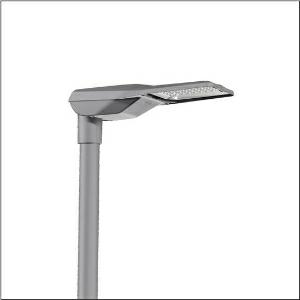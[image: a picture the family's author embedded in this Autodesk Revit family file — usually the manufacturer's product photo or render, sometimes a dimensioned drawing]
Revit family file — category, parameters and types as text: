
# Revit family: streetlight_sl_21_iq_mini___p1_0a_5xe2a31d08hb_09ea
name_source: partatom
category: Lighting Fixtures
units: mm (PartAtom-declared; Revit-internal decimal feet)

## family parameters
Cut with Voids When Loaded = No
Host = Face
Light Source = No
Part Type = Normal
Room Calculation Point = No
Round Connector Dimension = Use Diameter
Shared = No

## types (1)
- --- (1 x LED, 9450 lm, 70.9 W, 3000K)
    Apparent Load = 71 VA
    CIE Flux Codes = 21 50 90 100 100
    Color Rendering = 70
    Color Temperature = 3000K
    Default Elevation = 1800 mm
    Description = Streetlight SL 21 mini, mast luminaire, primary light control with lens, of PMMA, primary optical cover: cover, of toughened safety glass, transparent, light distribution: P1.0a, light emission: direct distribution, primary light characteristic: asymmetric, installation type: post-top, side-entry, LED, High Power LED, rated luminous flux: 9.450lm, luminous efficacy: 133lm/W, light colour: 730, colour temperature: 3000K, control gear: ECG iQ, control: Auto-Match, Temp-Guard, Lumen-Switch, Night-Set, Smart-Wire, Light-Fading, Desk-Remote (wireless, voltage-free reading and setting of iQ features in the workshop via application-optimized NFC function/RFID function), optimised constant luminous flux control (CLO 2.0), mains connection: 220..240V, AC, 50/60Hz, start of lifetime: 71W, end of lifetime: 75W, reduction: 31W, luminaire housing, of diecast aluminium, powder-coated, Siteco® metallic grey (DB 702S), corrosivity category C5 according to DIN EN ISO 12944, length: 628mm, width: 235mm, height: 110mm, spigot size: 60/76mm (post-top) and 42/60/76mm (side-entry), mast flange for spigot size: 42mm: 5XC10008XM4, 60mm: 5XC10008XM2, 76/60mm: 5XC10108XM1, protection rating (complete): IP66, insulation class (complete): insulation class II (safety insulation), certification: CE, ENEC, VDE, impact resistance: IK09, permissible operating ambient temperature for outdoor applications: -40..+50°C, standard-compliant lighting for roads and squares, packaging unit: 1 piece

Light Distribution: P1.0a
    Height = 110 mm
    Lamp = 1 x LED
    Lamp Light Flux = 9450 lm
    Lamp Power = 70.9 W
    Lamp count = 1
    Length = 625 mm
    Luminous efficacy = 133 lm/W
    Manufacturer = Siteco
    ModVariant = No
    Model = 5XE2A31D08HB
    Number of Poles = 1
    OnlyDefault = Yes
    Power Factor = 1
    Product Name = Streetlight SL 21 iQ mini | P1.0a
    Product group = mast luminaire | pylon top
    ProductGroupID = 6100
    Protection Class = Protection class II
    Protection Degree = IP 66
    RLX_Detail_Level = 1
    RlxData = <blob elided: 103601 chars, md5=19543abd>
    Socket = socket
    Standby Power = 0 W
    System Light Flux = 9450 lm
    System Power = 71 W
    Type Comments = factory setting: luminous flux: 100 % | dim-lin: 254 | 711 mA
    Type Image = l_1003519.jpg
    URL = http://relux.com
    VarID = @adj_068961
    Voltage = 0 V
    Weight = 0.00 kg
    Width = 234 mm

## geometry (parser evidence)
native form markers: Blend x4, Sweep x11
no freeform markers — native parametric forms only
